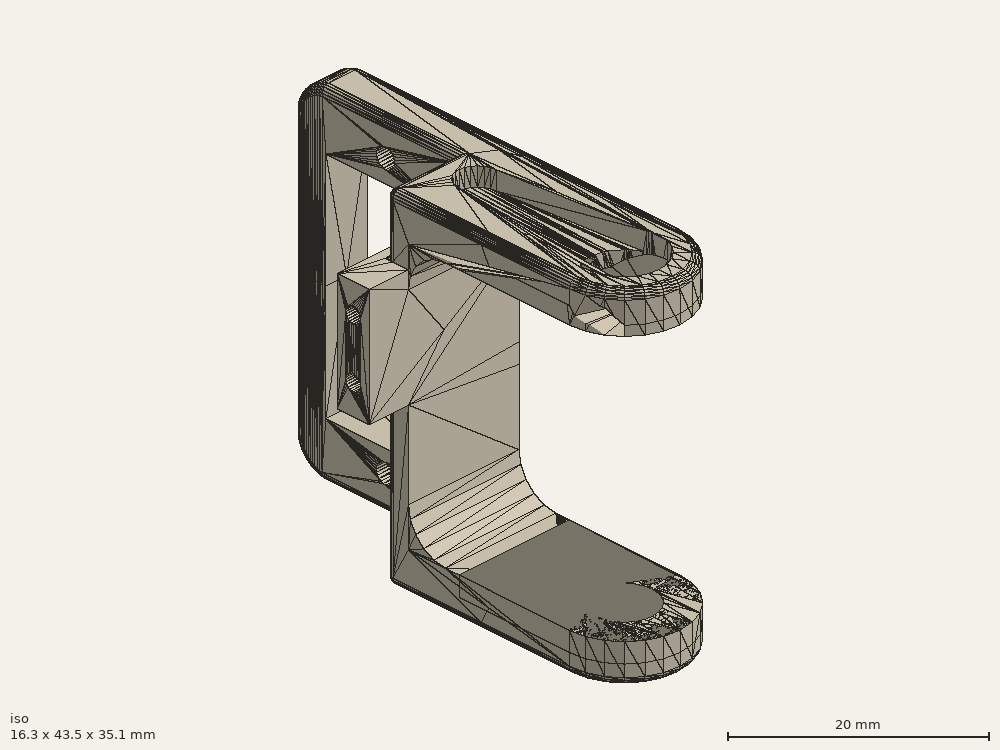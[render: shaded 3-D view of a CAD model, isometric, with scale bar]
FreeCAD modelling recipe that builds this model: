
FCSTD DOCUMENT  (FreeCAD 1.0R39319 (Git))
Label: coxa_r_new
License: All rights reserved
LicenseURL: https://en.wikipedia.org/wiki/All_rights_reserved
objects: Mesh::Feature×1, Part::Feature×1, PartDesign::FeatureBase×1, Sketcher::SketchObject×1, PartDesign::Pocket×1, PartDesign::Body×1
note: 9 computed .brp shape members not serialized (recipe doc carries the construction recipe); baked Part::Feature solids carry a one-line shape summary decoded from their .brp

FEATURE [Mesh::Feature] coxa_r
FEATURE [Part::Feature] Solid_from_mesh
  shape: bbox 16.47 x 43.71 x 35.31 mm, 2388 faces (baked)
FEATURE [PartDesign::FeatureBase] BaseFeature
  BaseFeature = -> Solid_from_mesh
  Suppressed = false
FEATURE [Sketcher::SketchObject] Sketch
  ArcFitTolerance = 1e-06
  AttachmentOffset = pos=(0,0,153) rot=(0,0,1;0rad)
  AttachmentSupport = -> [YZ_Plane]
  FullyConstrained = false
  MakeInternals = false
  MapMode = 5
  Placement = pos=(153,0,0) rot=(0.57735,0.57735,0.57735;2.0944rad)
  sketch-geometry (8):
    g0: LineSegment StartX=89.1733 StartY=-1.17616 StartZ=0 EndX=107.173 EndY=-1.17616 EndZ=0
    g1: LineSegment StartX=107.173 StartY=-1.17616 StartZ=0 EndX=107.173 EndY=0.823843 EndZ=0
    g2: LineSegment StartX=107.173 StartY=0.823843 StartZ=0 EndX=89.1733 EndY=0.823843 EndZ=0
    g3: LineSegment StartX=89.1733 StartY=0.823843 StartZ=0 EndX=89.1733 EndY=-1.17616 EndZ=0
    g4: LineSegment StartX=89.1896 StartY=27.8902 StartZ=0 EndX=107.19 EndY=27.8902 EndZ=0
    g5: LineSegment StartX=107.19 StartY=27.8902 StartZ=0 EndX=107.19 EndY=28.8902 EndZ=0
    g6: LineSegment StartX=107.19 StartY=28.8902 StartZ=0 EndX=89.1896 EndY=28.8902 EndZ=0
    g7: LineSegment StartX=89.1896 StartY=28.8902 StartZ=0 EndX=89.1896 EndY=27.8902 EndZ=0
  constraints (20):
    c: Coincident(g0,g1)
    c: Coincident(g1,g2)
    c: Coincident(g2,g3)
    c: Coincident(g3,g0)
    c: Horizontal(g0)
    c: Horizontal(g2)
    c: Vertical(g1)
    c: Vertical(g3)
    c: DistanceX(g2,g2) = 18
    c: DistanceY(g3,g3) = 2
    c: Coincident(g4,g5)
    c: Coincident(g5,g6)
    c: Coincident(g6,g7)
    c: Coincident(g7,g4)
    c: Horizontal(g4)
    c: Horizontal(g6)
    c: Vertical(g5)
    c: Vertical(g7)
    c: DistanceX(g4,g4) = 18
    c: DistanceY(g7,g7) = 1
FEATURE [PartDesign::Pocket] Pocket
  BaseFeature = -> BaseFeature
  Direction = (-1,0,0)
  Length = 16
  Length2 = 5
  Profile = -> Sketch
  ReferenceAxis = -> Sketch [N_Axis]
  Refine = true
  Reversed = true
  Suppressed = false
  Type = 0
FEATURE [PartDesign::Body] Body_from_mesh
  AllowCompound = false
  BaseFeature = -> Solid_from_mesh
  Group = -> [BaseFeature,Sketch,Pocket]
  Origin = -> Origin
  Tip = -> Pocket
